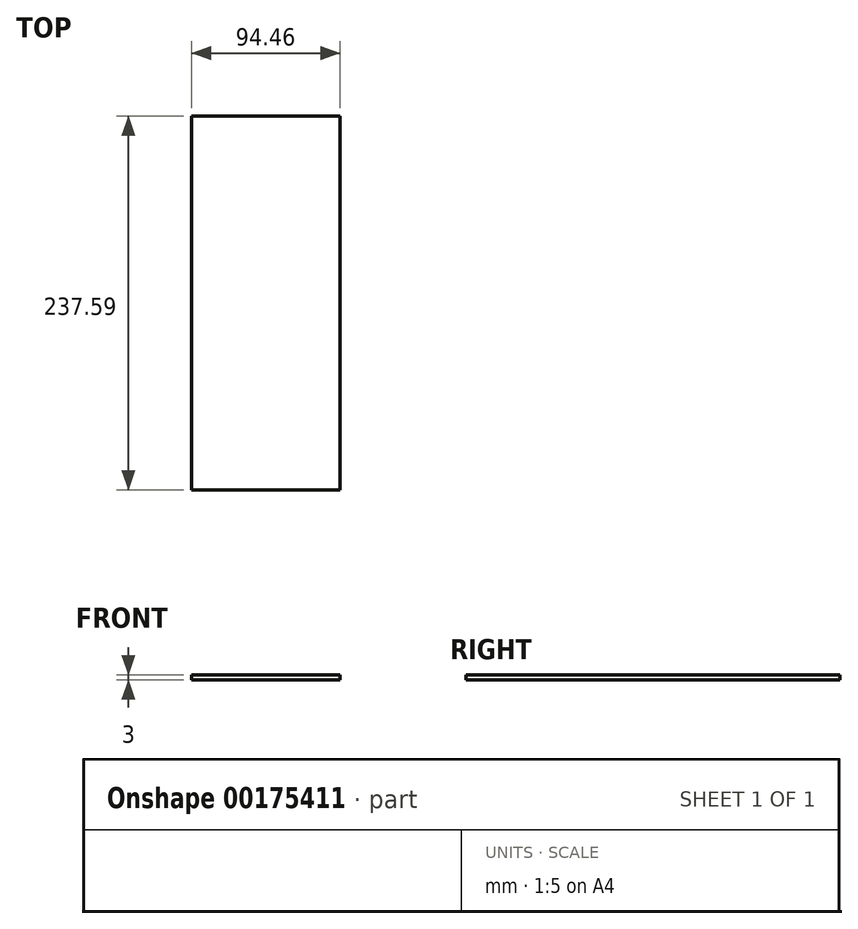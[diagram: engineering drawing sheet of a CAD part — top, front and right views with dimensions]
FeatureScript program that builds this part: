
annotation { "Feature Type Name" : "Feature", "Feature Type Description" : "" }
export const myFeature = defineFeature(function(context is Context, id is Id, definition is map)
    precondition{}
    {
        {
            var Q0;
            Q0=qCreatedBy(makeId("Top.planeOp"),FACE);
            var sketch = newSketch(context, id + "F0", { "sketchPlane" : qUnion([Q0])});
            skLineSegment(sketch, "E0.bottom", {"start": v(0, -237.59) * mm, "end": v(94.46, -237.59) * mm});
            skLineSegment(sketch, "E0.top", {"start": v(0, 0) * mm, "end": v(94.46, 0) * mm});
            skLineSegment(sketch, "E0.left", {"start": v(0, -237.59) * mm, "end": v(0, 0) * mm});
            skLineSegment(sketch, "E0.right", {"start": v(94.46, -237.59) * mm, "end": v(94.46, 0) * mm});
            skSolve(sketch);
        }
        {
            var Q0;
            Q0 = qSketchRegion(id + "F0", true);
            extrude(context, id + "F1", {"entities" : qUnion([Q0]), "depth" : 3 * mm});
        }
    });
